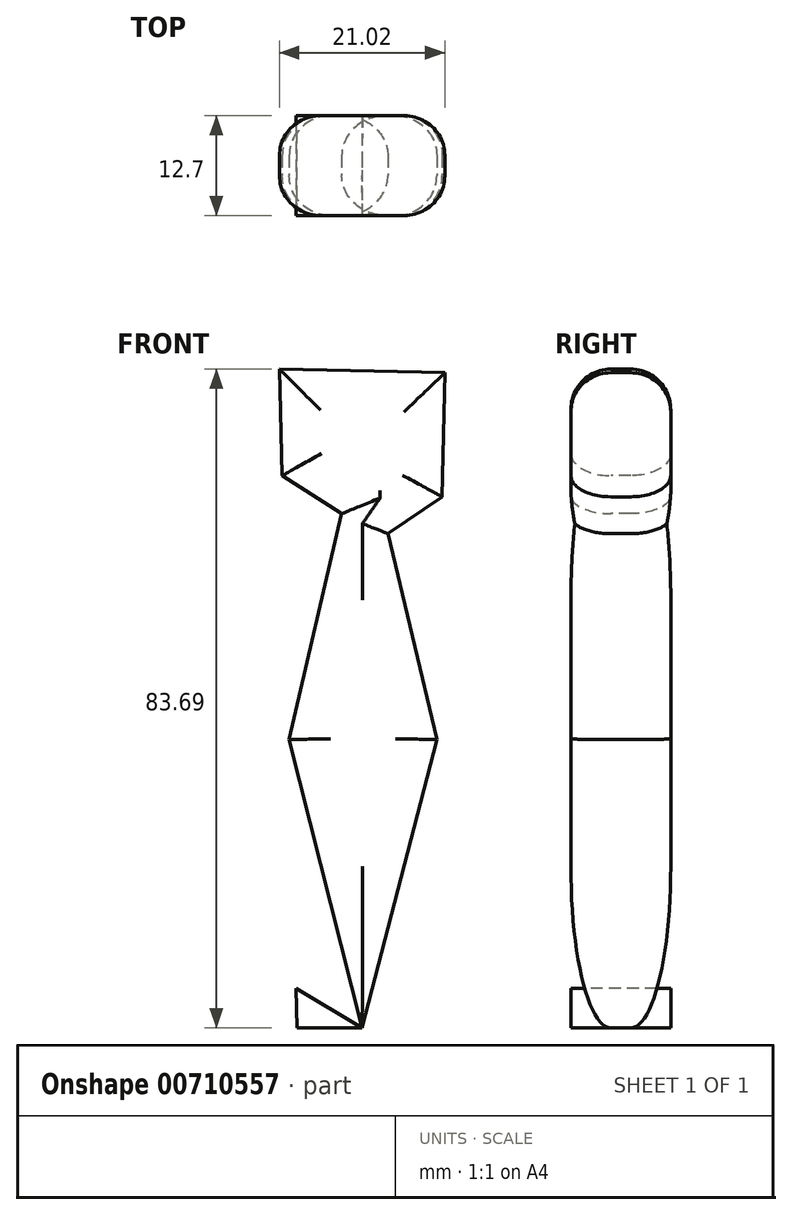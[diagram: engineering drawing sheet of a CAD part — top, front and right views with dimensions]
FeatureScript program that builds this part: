
annotation { "Feature Type Name" : "Feature", "Feature Type Description" : "" }
export const myFeature = defineFeature(function(context is Context, id is Id, definition is map)
    precondition{}
    {
        {
            var Q0;
            Q0=qCreatedBy(makeId("Front.planeOp"),FACE);
            var sketch = newSketch(context, id + "F0", { "sketchPlane" : qUnion([Q0])});
            skLineSegment(sketch, "E0", {"start": v(0, -8.4) * mm, "end": v(-10.52, -8.17) * mm});
            skLineSegment(sketch, "E1", {"start": v(-10.52, -8.17) * mm, "end": v(10.5, -8.63) * mm});
            skLineSegment(sketch, "E2", {"start": v(10.5, -8.63) * mm, "end": v(0, -8.4) * mm});
            skLineSegment(sketch, "E3", {"start": v(-10.52, -8.17) * mm, "end": v(-8.3, -91.86) * mm});
            skLineSegment(sketch, "E4", {"start": v(-8.3, -91.86) * mm, "end": v(-10.52, -8.17) * mm});
            skLineSegment(sketch, "E5", {"start": v(10.5, -8.63) * mm, "end": v(8.67, -91.86) * mm});
            skLineSegment(sketch, "E6", {"start": v(8.67, -91.86) * mm, "end": v(-8.3, -91.86) * mm});
            skSolve(sketch);
        }
        {
            var Q0;
            Q0=makeQuery(id+"F0.imprint","IMPRINT",FACE,{"disambiguationData":[TD([[makeQuery(id+"F0.imprint","IMPRINT",EDGE,{"derivedFrom":sQuery(id+"F0.wireOp",EDGE,"E1")}),-1.0]])]});
            extrude(context, id + "F1", {"entities" : qUnion([Q0]), "depth" : 6.35 * mm, "offsetDistance" : 25.4 * mm});
        }
        {
            var Q0;
            Q0=makeQuery(id+"F1.opExtrude","CAP_FACE",FACE,{"disambiguationData":[OSD([sQuery(id+"F0.wireOp",EDGE,"E1"),sQuery(id+"F0.wireOp",EDGE,"E2"),sQuery(id+"F0.wireOp",EDGE,"E4"),sQuery(id+"F0.wireOp",EDGE,"E5"),sQuery(id+"F0.wireOp",EDGE,"E6")])],"isStart":true});
            extrude(context, id + "F2", {"entities" : qUnion([Q0]), "operationType" : NewBodyOperationType.ADD, "depth" : 6.35 * mm, "offsetDistance" : 25.4 * mm});
        }
        {
            var Q0;
            Q0=makeQuery(id+"F1.opExtrude","CAP_FACE",FACE,{"disambiguationData":[OSD([sQuery(id+"F0.wireOp",EDGE,"E1"),sQuery(id+"F0.wireOp",EDGE,"E2"),sQuery(id+"F0.wireOp",EDGE,"E4"),sQuery(id+"F0.wireOp",EDGE,"E5"),sQuery(id+"F0.wireOp",EDGE,"E6")])],"isStart":false});
            var sketch = newSketch(context, id + "F3", { "sketchPlane" : qUnion([Q0])});
            skLineSegment(sketch, "E7", {"start": v(0, -12.7) * mm, "end": v(-8.4, -8.21) * mm});
            skLineSegment(sketch, "E8", {"start": v(-8.4, -8.21) * mm, "end": v(0, -12.7) * mm});
            skLineSegment(sketch, "E9", {"start": v(0, -15.3) * mm, "end": v(-10.47, -10.2) * mm});
            skLineSegment(sketch, "E10", {"start": v(-10.47, -10.2) * mm, "end": v(0, -15.3) * mm});
            skLineSegment(sketch, "E11", {"start": v(0, -15.3) * mm, "end": v(-9.27, -55.2) * mm});
            skLineSegment(sketch, "E12", {"start": v(-9.27, -55.2) * mm, "end": v(0, -91.86) * mm});
            skLineSegment(sketch, "E13", {"start": v(0, -91.86) * mm, "end": v(9.48, -55.2) * mm});
            skLineSegment(sketch, "E14", {"start": v(9.48, -55.2) * mm, "end": v(0, -15.3) * mm});
            skLineSegment(sketch, "E15", {"start": v(2.66, -26.5) * mm, "end": v(10.21, -21.68) * mm});
            skLineSegment(sketch, "E16", {"start": v(10.21, -21.68) * mm, "end": v(2.66, -26.5) * mm});
            skLineSegment(sketch, "E17", {"start": v(3.27, -29.07) * mm, "end": v(10.15, -24.4) * mm});
            skLineSegment(sketch, "E18", {"start": v(0, -91.86) * mm, "end": v(8.78, -86.64) * mm});
            skLineSegment(sketch, "E19", {"start": v(1, -88.02) * mm, "end": v(8.87, -82.55) * mm});
            skLineSegment(sketch, "E20", {"start": v(4.2, -75.62) * mm, "end": v(9.08, -73.04) * mm});
            skLineSegment(sketch, "E21", {"start": v(3.23, -79.36) * mm, "end": v(9.02, -75.93) * mm});
            skLineSegment(sketch, "E22", {"start": v(0, -44.6) * mm, "end": v(0, -50.7) * mm});
            skLineSegment(sketch, "E23.MirrorCS", {"start": v(-10.21, -21.68) * mm, "end": v(-2.66, -26.5) * mm});
            skLineSegment(sketch, "E24.MirrorCS", {"start": v(-3.27, -29.07) * mm, "end": v(-10.15, -24.4) * mm});
            skLineSegment(sketch, "E25.MirrorCS", {"start": v(10.47, -10.2) * mm, "end": v(0, -15.3) * mm});
            skLineSegment(sketch, "E26.MirrorCS", {"start": v(8.4, -8.21) * mm, "end": v(0, -12.7) * mm});
            skLineSegment(sketch, "E27.MirrorCS", {"start": v(-4.2, -75.62) * mm, "end": v(-9.08, -73.04) * mm});
            skLineSegment(sketch, "E28.MirrorCS", {"start": v(-3.23, -79.36) * mm, "end": v(-9.02, -75.93) * mm});
            skLineSegment(sketch, "E29.MirrorCS", {"start": v(-1, -88.02) * mm, "end": v(-8.87, -82.55) * mm});
            skLineSegment(sketch, "E30.MirrorCS", {"start": v(0, -91.86) * mm, "end": v(-8.78, -86.64) * mm});
            skLineSegment(sketch, "E31", {"start": v(-3.46, -28.94) * mm, "end": v(-3.21, -29.1) * mm});
            skLineSegment(sketch, "E32", {"start": v(-2.67, -26.5) * mm, "end": v(-2.61, -26.53) * mm});
            skLineSegment(sketch, "E33", {"start": v(-4.27, -75.58) * mm, "end": v(-4.1, -75.67) * mm});
            skLineSegment(sketch, "E34", {"start": v(-3.31, -79.31) * mm, "end": v(-3.15, -79.4) * mm});
            skLineSegment(sketch, "E35", {"start": v(-1, -88.01) * mm, "end": v(-0.97, -88.04) * mm});
            skSolve(sketch);
        }
        {
            var Q0;
            {var subQ3=sQuery(id+"F3.wireOp",EDGE,"E20");Q0=makeQuery(id+"F3.imprint","IMPRINT",FACE,{"disambiguationData":[TD([[makeQuery(id+"F3.imprint","IMPRINT",EDGE,{"derivedFrom":subQ3}),1.0]])]});}
            var Q1;
            {var subQ0=sQuery(id+"F3.wireOp",EDGE,"E20");Q1=makeQuery(id+"F3.imprint","IMPRINT",FACE,{"disambiguationData":[TD([[makeQuery(id+"F3.imprint","IMPRINT",EDGE,{"derivedFrom":subQ0}),-1.0]])]});}
            var Q2;
            {var subQ0=sQuery(id+"F3.wireOp",EDGE,"E19");Q2=makeQuery(id+"F3.imprint","IMPRINT",FACE,{"disambiguationData":[TD([[makeQuery(id+"F3.imprint","IMPRINT",EDGE,{"derivedFrom":subQ0}),1.0]])]});}
            var Q3;
            {var subQ0=sQuery(id+"F3.wireOp",EDGE,"E18");Q3=makeQuery(id+"F3.imprint","IMPRINT",FACE,{"disambiguationData":[TD([[makeQuery(id+"F3.imprint","IMPRINT",EDGE,{"derivedFrom":subQ0}),1.0]])]});}
            var Q4;
            {var subQ0=sQuery(id+"F3.wireOp",EDGE,"E18");Q4=makeQuery(id+"F3.imprint","IMPRINT",FACE,{"disambiguationData":[TD([[makeQuery(id+"F3.imprint","IMPRINT",EDGE,{"derivedFrom":subQ0}),-1.0]])]});}
            var Q5;
            {var subQ1=makeQuery(id+"F1.opExtrude","CAP_EDGE",EDGE,{"disambiguationData":[OSD([sQuery(id+"F0.wireOp",EDGE,"E6")])],"isStart":false});var subQ3=makeQuery(id+"F1.opExtrude","CAP_EDGE",EDGE,{"disambiguationData":[OSD([sQuery(id+"F0.wireOp",EDGE,"E4")])],"isStart":false});var subQ5=makeQuery(id+"F3.imprint","INTERSECT",VERTEX,{"derivedFrom":[subQ3,subQ1]});Q5=makeQuery(id+"F3.imprint","IMPRINT",FACE,{"disambiguationData":[TD([[makeQuery(id+"F3.imprint","IMPRINT",EDGE,{"disambiguationData":[TD([[subQ5,-1.0]])],"derivedFrom":subQ3}),-1.0]])]});}
            var Q6;
            {var subQ7=sQuery(id+"F3.wireOp",EDGE,"E35");var subQ9=makeQuery(id+"F3.imprint","IMPRINT",VERTEX,{"derivedFrom":subQ7});Q6=makeQuery(id+"F3.imprint","IMPRINT",FACE,{"disambiguationData":[TD([[makeQuery(id+"F3.imprint","IMPRINT",EDGE,{"disambiguationData":[TD([[subQ9,1.0]])],"derivedFrom":subQ7}),-1.0]])]});}
            var Q7;
            {var subQ0=sQuery(id+"F3.wireOp",EDGE,"E34");var subQ3=makeQuery(id+"F3.imprint","IMPRINT",VERTEX,{"derivedFrom":subQ0});Q7=makeQuery(id+"F3.imprint","IMPRINT",FACE,{"disambiguationData":[TD([[makeQuery(id+"F3.imprint","IMPRINT",EDGE,{"disambiguationData":[TD([[subQ3,1.0]])],"derivedFrom":subQ0}),-1.0]])]});}
            var Q8;
            {var subQ0=sQuery(id+"F3.wireOp",EDGE,"E33");var subQ3=makeQuery(id+"F3.imprint","IMPRINT",VERTEX,{"derivedFrom":subQ0});Q8=makeQuery(id+"F3.imprint","IMPRINT",FACE,{"disambiguationData":[TD([[makeQuery(id+"F3.imprint","IMPRINT",EDGE,{"disambiguationData":[TD([[subQ3,1.0]])],"derivedFrom":subQ0}),-1.0]])]});}
            var Q9;
            {var subQ0=sQuery(id+"F3.wireOp",EDGE,"E33");var subQ3=makeQuery(id+"F3.imprint","IMPRINT",VERTEX,{"derivedFrom":subQ0});Q9=makeQuery(id+"F3.imprint","IMPRINT",FACE,{"disambiguationData":[TD([[makeQuery(id+"F3.imprint","IMPRINT",EDGE,{"disambiguationData":[TD([[subQ3,1.0]])],"derivedFrom":subQ0}),1.0]])]});}
            var Q10;
            {var subQ3=sQuery(id+"F3.wireOp",EDGE,"E17");Q10=makeQuery(id+"F3.imprint","IMPRINT",FACE,{"disambiguationData":[TD([[makeQuery(id+"F3.imprint","IMPRINT",EDGE,{"derivedFrom":subQ3}),-1.0]])]});}
            var Q11;
            {var subQ0=sQuery(id+"F3.wireOp",EDGE,"E16");Q11=makeQuery(id+"F3.imprint","IMPRINT",FACE,{"disambiguationData":[TD([[makeQuery(id+"F3.imprint","IMPRINT",EDGE,{"derivedFrom":subQ0}),1.0]])]});}
            var Q12;
            {var subQ3=sQuery(id+"F3.wireOp",EDGE,"E16");Q12=makeQuery(id+"F3.imprint","IMPRINT",FACE,{"disambiguationData":[TD([[makeQuery(id+"F3.imprint","IMPRINT",EDGE,{"derivedFrom":subQ3}),-1.0]])]});}
            var Q13;
            {var subQ5=sQuery(id+"F3.wireOp",EDGE,"E8");Q13=makeQuery(id+"F3.imprint","IMPRINT",FACE,{"disambiguationData":[TD([[makeQuery(id+"F3.imprint","IMPRINT",EDGE,{"derivedFrom":subQ5}),-1.0]])]});}
            var Q14;
            {var subQ0=sQuery(id+"F3.wireOp",EDGE,"E8");Q14=makeQuery(id+"F3.imprint","IMPRINT",FACE,{"disambiguationData":[TD([[makeQuery(id+"F3.imprint","IMPRINT",EDGE,{"derivedFrom":subQ0}),1.0]])]});}
            var Q15;
            {var subQ8=sQuery(id+"F3.wireOp",EDGE,"E10");Q15=makeQuery(id+"F3.imprint","IMPRINT",FACE,{"disambiguationData":[TD([[makeQuery(id+"F3.imprint","IMPRINT",EDGE,{"derivedFrom":subQ8}),-1.0]])]});}
            var Q16;
            {var subQ0=sQuery(id+"F3.wireOp",EDGE,"E31");var subQ3=makeQuery(id+"F3.imprint","IMPRINT",VERTEX,{"derivedFrom":subQ0});Q16=makeQuery(id+"F3.imprint","IMPRINT",FACE,{"disambiguationData":[TD([[makeQuery(id+"F3.imprint","IMPRINT",EDGE,{"disambiguationData":[TD([[subQ3,1.0]])],"derivedFrom":subQ0}),1.0]])]});}
            var Q17;
            {var subQ0=sQuery(id+"F3.wireOp",EDGE,"E31");var subQ3=makeQuery(id+"F3.imprint","IMPRINT",VERTEX,{"derivedFrom":subQ0});Q17=makeQuery(id+"F3.imprint","IMPRINT",FACE,{"disambiguationData":[TD([[makeQuery(id+"F3.imprint","IMPRINT",EDGE,{"disambiguationData":[TD([[subQ3,1.0]])],"derivedFrom":subQ0}),-1.0]])]});}
            extrude(context, id + "F4", {"entities" : qUnion([Q0, Q1, Q2, Q3, Q4, Q5, Q6, Q7, Q8, Q9, Q10, Q11, Q12, Q13, Q14, Q15, Q16, Q17]), "operationType" : NewBodyOperationType.REMOVE, "oppositeDirection" : true, "depth" : 25.4 * mm, "offsetDistance" : 25.4 * mm});
        }
        {
            var Q0;
            Q0=makeQuery(id+"F1.opExtrude","CAP_FACE",FACE,{"disambiguationData":[OSD([sQuery(id+"F0.wireOp",EDGE,"E1"),sQuery(id+"F0.wireOp",EDGE,"E2"),sQuery(id+"F0.wireOp",EDGE,"E4"),sQuery(id+"F0.wireOp",EDGE,"E5"),sQuery(id+"F0.wireOp",EDGE,"E6")])],"isStart":false});
            var Q1;
            Q1=makeQuery(id+"F2.opExtrude","CAP_FACE",FACE,{"disambiguationData":[OSD([sQuery(id+"F0.wireOp",EDGE,"E1"),sQuery(id+"F0.wireOp",EDGE,"E2"),sQuery(id+"F0.wireOp",EDGE,"E4"),sQuery(id+"F0.wireOp",EDGE,"E5"),sQuery(id+"F0.wireOp",EDGE,"E6")])],"isStart":false});
            fillet(context, id + "F5", {"entities" : qUnion([Q0, Q1]), "radius" : 5.08 * mm, "tangentPropagation" : true, "allowEdgeOverflow" : false});
        }
    });
